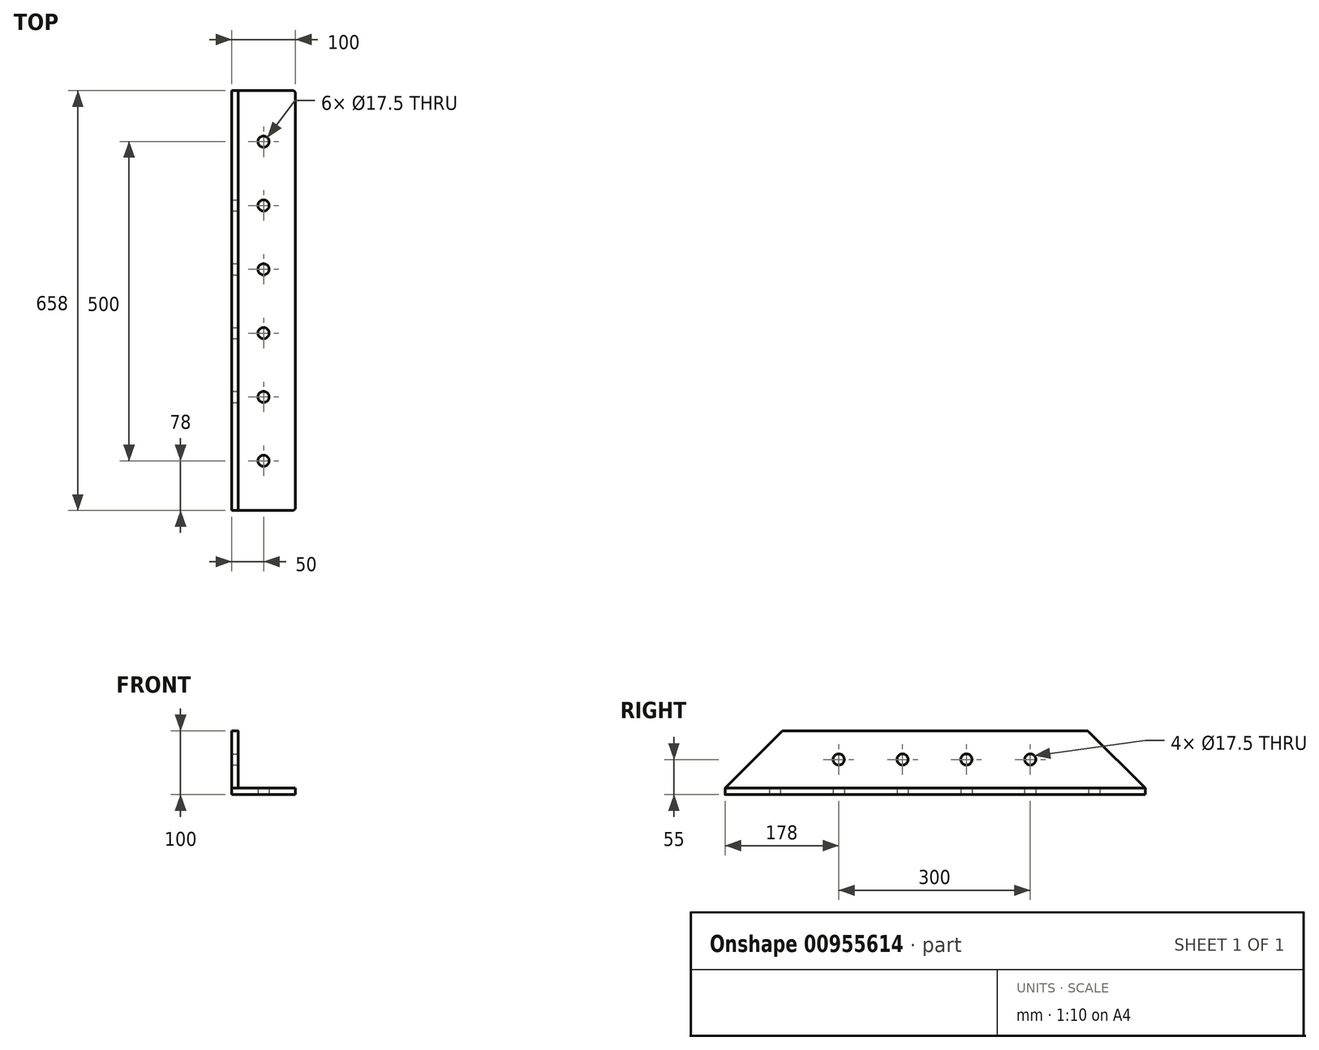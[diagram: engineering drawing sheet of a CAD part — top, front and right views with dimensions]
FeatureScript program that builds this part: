
annotation { "Feature Type Name" : "Feature", "Feature Type Description" : "" }
export const myFeature = defineFeature(function(context is Context, id is Id, definition is map)
    precondition{}
    {
        {
            var Q0;
            Q0=qCreatedBy(makeId("Front.planeOp"),FACE);
            var sketch = newSketch(context, id + "F0", { "sketchPlane" : qUnion([Q0])});
            skLineSegment(sketch, "E0", {"start": v(0, 0) * mm, "end": v(0, 100) * mm});
            skLineSegment(sketch, "E1", {"start": v(0, 100) * mm, "end": v(10, 100) * mm});
            skLineSegment(sketch, "E2", {"start": v(10, 100) * mm, "end": v(10, 10) * mm});
            skLineSegment(sketch, "E3", {"start": v(10, 10) * mm, "end": v(100, 10) * mm});
            skLineSegment(sketch, "E4", {"start": v(100, 10) * mm, "end": v(100, 0) * mm});
            skLineSegment(sketch, "E5", {"start": v(100, 0) * mm, "end": v(0, 0) * mm});
            skSolve(sketch);
        }
        {
            var Q0;
            Q0 = qSketchRegion(id + "F0", true);
            extrude(context, id + "F1", {"entities" : qUnion([Q0]), "depth" : 658 * mm, "offsetDistance" : 25 * mm});
        }
        {
            var Q0;
            Q0=makeQuery(id+"F1.opExtrude","SWEPT_FACE",FACE,{"disambiguationData":[OSD([sQuery(id+"F0.wireOp",EDGE,"E2")])]});
            var sketch = newSketch(context, id + "F2", { "sketchPlane" : qUnion([Q0])});
            skLineSegment(sketch, "E6", {"start": v(0, 55) * mm, "end": v(-180, 55) * mm});
            skCircle(sketch, "E7", {"center": v(-180, 55) * mm, "radius": 8 * mm});
            skCircle(sketch, "E8.1.0.0", {"center": v(-280, 55) * mm, "radius": 8 * mm});
            skCircle(sketch, "E8.2.0.0", {"center": v(-380, 55) * mm, "radius": 8 * mm});
            skCircle(sketch, "E8.3.0.0", {"center": v(-480, 55) * mm, "radius": 8 * mm});
            skLineSegment(sketch, "E8.direction1", {"start": v(-180, 55) * mm, "end": v(-280, 55) * mm, "construction": true});
            skSolve(sketch);
        }
        {
            var Q0;
            Q0=sQuery(id+"F2.wireOp",VERTEX,"E6.end");
            var Q1;
            Q1=sQuery(id+"F2.wireOp",VERTEX,"E8.direction1.end");
            var Q2;
            Q2=sQuery(id+"F2.wireOp",VERTEX,"E8.2.0.0.center");
            var Q3;
            Q3=sQuery(id+"F2.wireOp",VERTEX,"E8.3.0.0.center");
            var Q4;
            Q4=makeQuery(id+"F1.opExtrude","SWEPT_BODY",BODY,{"disambiguationData":[OSD([sQuery(id+"F0.wireOp",EDGE,"E0"),sQuery(id+"F0.wireOp",EDGE,"E1"),sQuery(id+"F0.wireOp",EDGE,"E2"),sQuery(id+"F0.wireOp",EDGE,"E3"),sQuery(id+"F0.wireOp",EDGE,"E4"),sQuery(id+"F0.wireOp",EDGE,"E5")])]});
            hole(context, id + "F3", {"style" : HoleStyle.SIMPLE, "endStyle" : HoleEndStyle.THROUGH, "standardTappedOrClearance" : lookupTablePath({ "standard" : "ISO", "engagement" : "75%", "pitch" : "2.5 mm", "size" : "M20", "type" : "Tapped" }), "standardBlindInLast" : lookupTablePath({ "standard" : "ISO", "fit" : "Normal", "engagement" : "75%", "pitch" : "2.5 mm", "size" : "M20", "type" : "Clearance & tapped" }), "holeDiameter" : 17.5 * mm, "majorDiameter" : 20 * mm, "showTappedDepth" : true, "isTappedThrough" : true, "tappedDepth" : 14.75 * mm, "tapClearance" : 3, "locations" : qUnion([Q0, Q1, Q2, Q3]), "scope" : qUnion([Q4])});
        }
        {
            var Q0;
            Q0=qCreatedBy(makeId("Top.planeOp"),FACE);
            var sketch = newSketch(context, id + "F4", { "sketchPlane" : qUnion([Q0])});
            skLineSegment(sketch, "E9", {"start": v(0, 0) * mm, "end": v(50, 0) * mm});
            skLineSegment(sketch, "E10", {"start": v(50, 0) * mm, "end": v(50, -80) * mm});
            skCircle(sketch, "E11", {"center": v(50, -80) * mm, "radius": 9 * mm});
            skCircle(sketch, "E12.1.0.0", {"center": v(50, -180) * mm, "radius": 9 * mm});
            skCircle(sketch, "E12.2.0.0", {"center": v(50, -280) * mm, "radius": 9 * mm});
            skCircle(sketch, "E12.3.0.0", {"center": v(50, -380) * mm, "radius": 9 * mm});
            skCircle(sketch, "E12.4.0.0", {"center": v(50, -480) * mm, "radius": 9 * mm});
            skCircle(sketch, "E12.5.0.0", {"center": v(50, -580) * mm, "radius": 9 * mm});
            skLineSegment(sketch, "E12.direction1", {"start": v(50, -80) * mm, "end": v(50, -180) * mm, "construction": true});
            skSolve(sketch);
        }
        {
            var Q0;
            Q0=sQuery(id+"F4.wireOp",VERTEX,"E12.5.0.0.center");
            var Q1;
            Q1=sQuery(id+"F4.wireOp",VERTEX,"E12.4.0.0.center");
            var Q2;
            Q2=sQuery(id+"F4.wireOp",VERTEX,"E12.3.0.0.center");
            var Q3;
            Q3=sQuery(id+"F4.wireOp",VERTEX,"E12.2.0.0.center");
            var Q4;
            Q4=sQuery(id+"F4.wireOp",VERTEX,"E12.direction1.end");
            var Q5;
            Q5=sQuery(id+"F4.wireOp",VERTEX,"E10.end");
            var Q6;
            Q6=makeQuery(id+"F1.opExtrude","SWEPT_BODY",BODY,{"disambiguationData":[OSD([sQuery(id+"F0.wireOp",EDGE,"E0"),sQuery(id+"F0.wireOp",EDGE,"E1"),sQuery(id+"F0.wireOp",EDGE,"E2"),sQuery(id+"F0.wireOp",EDGE,"E3"),sQuery(id+"F0.wireOp",EDGE,"E4"),sQuery(id+"F0.wireOp",EDGE,"E5")])]});
            hole(context, id + "F5", {"style" : HoleStyle.SIMPLE, "endStyle" : HoleEndStyle.THROUGH, "oppositeDirection" : true, "standardTappedOrClearance" : lookupTablePath({ "fit" : "Normal", "standard" : "ISO", "size" : "M16", "type" : "Clearance" }), "standardBlindInLast" : lookupTablePath({ "fit" : "Normal", "standard" : "ISO", "engagement" : "75%", "pitch" : "2 mm", "size" : "M16", "type" : "Clearance & tapped" }), "holeDiameter" : 17.5 * mm, "majorDiameter" : 24 * mm, "isTappedThrough" : true, "tappedDepth" : 14.75 * mm, "tapClearance" : 3, "locations" : qUnion([Q0, Q1, Q2, Q3, Q4, Q5]), "scope" : qUnion([Q6])});
        }
        {
            var Q0;
            Q0=qCreatedBy(makeId("Top.planeOp"),FACE);
            cPlane(context, id + "F6", {"entities" : qUnion([Q0]), "cplaneType" : CPlaneType.OFFSET, "offset" : 10 * mm, "width" : 150 * mm, "height" : 150 * mm});
        }
        {
            var Q0;
            Q0=makeQuery(id+"F1.opExtrude","CAP_EDGE",EDGE,{"disambiguationData":[OSD([sQuery(id+"F0.wireOp",EDGE,"E1")])],"isStart":false});
            var Q1;
            Q1=makeQuery(id+"F1.opExtrude","CAP_EDGE",EDGE,{"disambiguationData":[OSD([sQuery(id+"F0.wireOp",EDGE,"E1")])],"isStart":true});
            chamfer(context, id + "F7", {"entities" : qUnion([Q0, Q1]), "width" : 90 * mm, "tangentPropagation" : true});
        }
        {
            var Q0;
            {var subQ0=sQuery(id+"F0.wireOp",EDGE,"E1");Q0=makeQuery(id+"F7.opChamfer","BLEND_EDGE",EDGE,{"blendedFrom":[makeQuery(id+"F1.opExtrude","CAP_EDGE",EDGE,{"disambiguationData":[OSD([subQ0])],"isStart":true}),makeQuery(id+"F1.opExtrude","SWEPT_FACE",FACE,{"disambiguationData":[OSD([subQ0])]})],"blendedInto":[makeQuery(id+"F1.opExtrude","SWEPT_FACE",FACE,{"disambiguationData":[OSD([subQ0])]})]});}
            var Q1;
            Q1=makeQuery(id+"F1.opExtrude","CAP_EDGE",EDGE,{"disambiguationData":[OSD([sQuery(id+"F0.wireOp",EDGE,"E4")])],"isStart":true});
            var Q2;
            {var subQ0=sQuery(id+"F0.wireOp",EDGE,"E1");Q2=makeQuery(id+"F7.opChamfer","BLEND_EDGE",EDGE,{"blendedFrom":[makeQuery(id+"F1.opExtrude","CAP_EDGE",EDGE,{"disambiguationData":[OSD([subQ0])],"isStart":false}),makeQuery(id+"F1.opExtrude","SWEPT_FACE",FACE,{"disambiguationData":[OSD([subQ0])]})],"blendedInto":[makeQuery(id+"F1.opExtrude","SWEPT_FACE",FACE,{"disambiguationData":[OSD([subQ0])]})]});}
            var Q3;
            Q3=makeQuery(id+"F1.opExtrude","CAP_EDGE",EDGE,{"disambiguationData":[OSD([sQuery(id+"F0.wireOp",EDGE,"E4")])],"isStart":false});
            fillet(context, id + "F8", {"entities" : qUnion([Q0, Q1, Q2, Q3]), "radius" : 5 * mm, "tangentPropagation" : true, "allowEdgeOverflow" : false});
        }
    });
